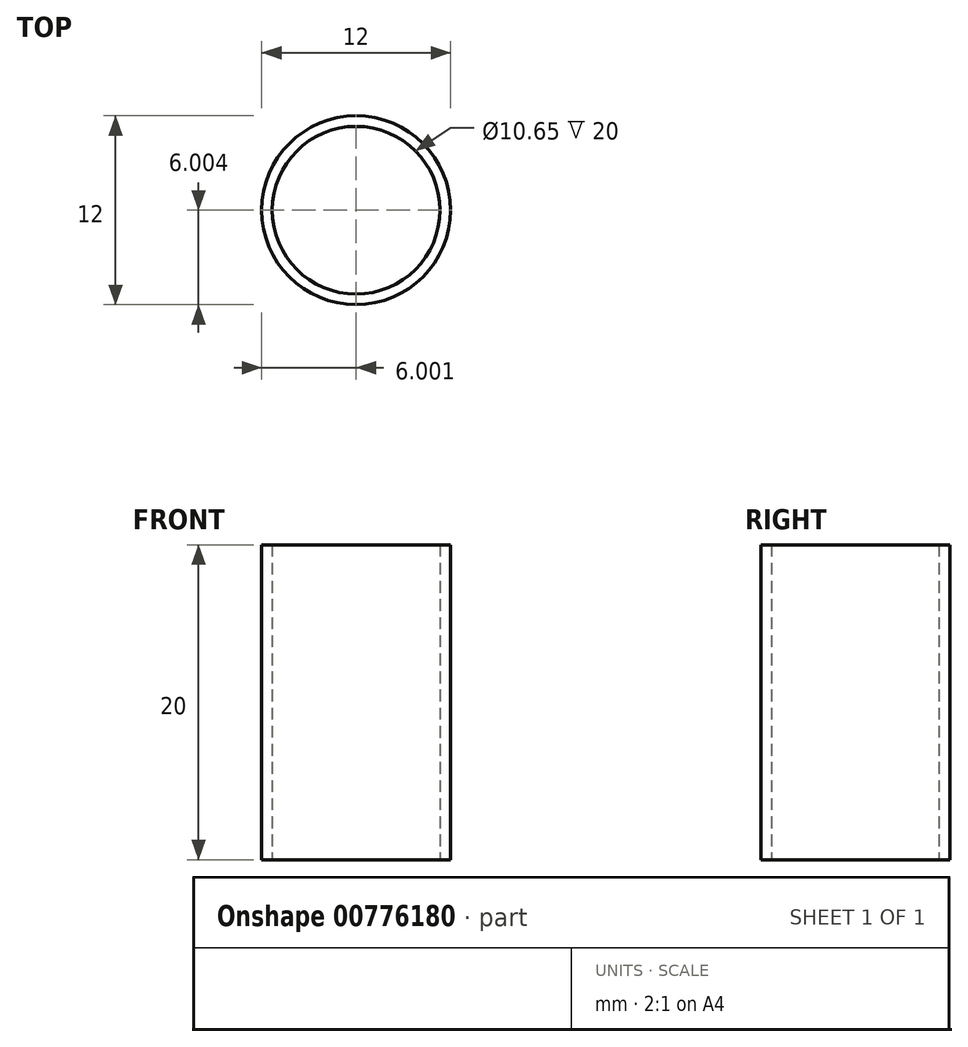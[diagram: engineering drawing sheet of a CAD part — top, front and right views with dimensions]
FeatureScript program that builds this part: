
annotation { "Feature Type Name" : "Feature", "Feature Type Description" : "" }
export const myFeature = defineFeature(function(context is Context, id is Id, definition is map)
    precondition{}
    {
        {
            var Q0;
            Q0=qCreatedBy(makeId("Top.planeOp"),FACE);
            var sketch = newSketch(context, id + "F0", { "sketchPlane" : qUnion([Q0])});
            skCircle(sketch, "E0", {"center": v(-38.96, 20.87) * mm, "radius": 6 * mm});
            skCircle(sketch, "E1", {"center": v(-38.96, 20.87) * mm, "radius": 5.33 * mm});
            skSolve(sketch);
        }
        {
            var Q0;
            Q0 = qSketchRegion(id + "F0", true);
            extrude(context, id + "F1", {"entities" : qUnion([Q0]), "depth" : 20 * mm, "offsetDistance" : 25 * mm});
        }
    });
